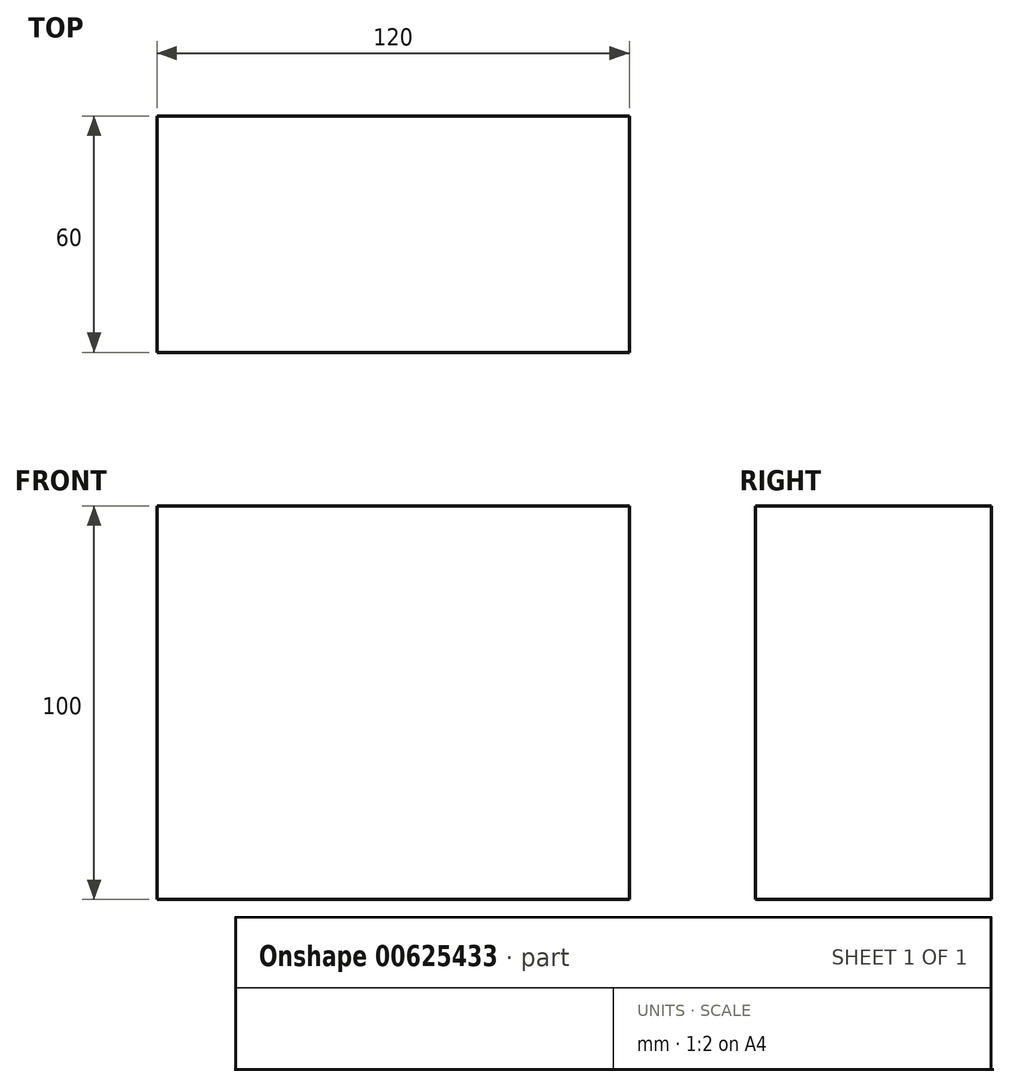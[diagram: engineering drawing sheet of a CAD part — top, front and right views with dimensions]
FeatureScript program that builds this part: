
annotation { "Feature Type Name" : "Feature", "Feature Type Description" : "" }
export const myFeature = defineFeature(function(context is Context, id is Id, definition is map)
    precondition{}
    {
        {
            var Q0;
            Q0=qCreatedBy(makeId("Front.planeOp"),FACE);
            var sketch = newSketch(context, id + "F0", { "sketchPlane" : qUnion([Q0])});
            skLineSegment(sketch, "E0.bottom", {"start": v(60, -50) * mm, "end": v(-60, -50) * mm});
            skLineSegment(sketch, "E0.top", {"start": v(60, 50) * mm, "end": v(-60, 50) * mm});
            skLineSegment(sketch, "E0.left", {"start": v(60, -50) * mm, "end": v(60, 50) * mm});
            skLineSegment(sketch, "E0.right", {"start": v(-60, -50) * mm, "end": v(-60, 50) * mm});
            skPoint(sketch, "E0.middle", {"position": v(0, 0) * mm});
            skSolve(sketch);
        }
        {
            var Q0;
            Q0=makeQuery(id+"F0.imprint","IMPRINT",FACE,{"disambiguationData":[TD([[makeQuery(id+"F0.imprint","IMPRINT",EDGE,{"derivedFrom":sQuery(id+"F0.wireOp",EDGE,"E0.bottom")}),-1.0]])]});
            extrude(context, id + "F1", {"entities" : qUnion([Q0]), "depth" : 60 * mm, "offsetDistance" : 25 * mm});
        }
    });
